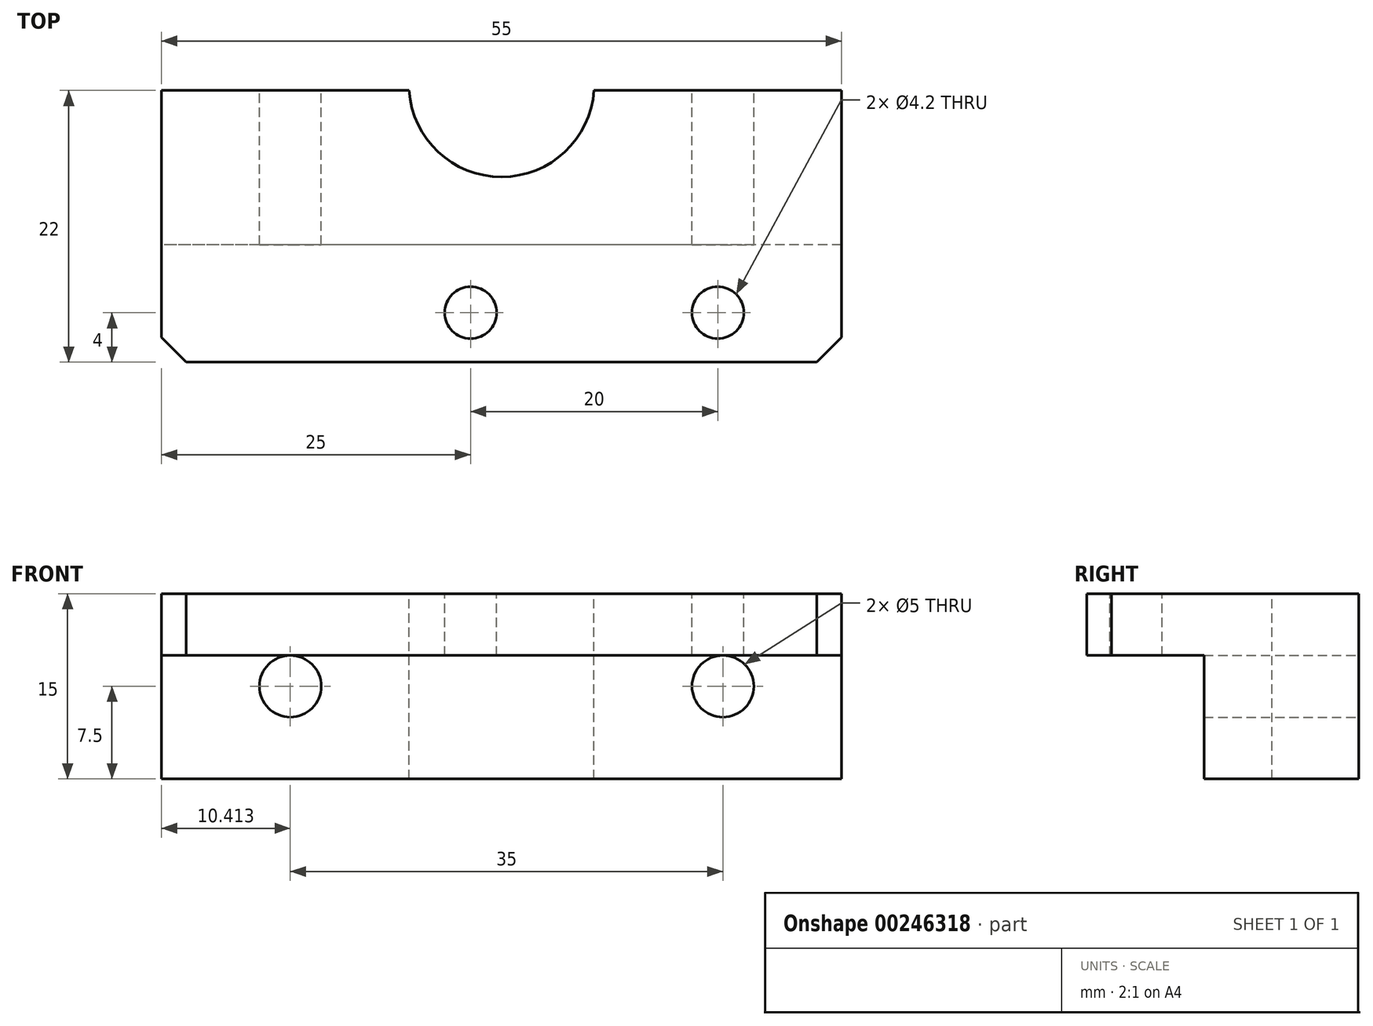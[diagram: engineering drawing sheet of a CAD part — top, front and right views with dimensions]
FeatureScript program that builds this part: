
annotation { "Feature Type Name" : "Feature", "Feature Type Description" : "" }
export const myFeature = defineFeature(function(context is Context, id is Id, definition is map)
    precondition{}
    {
        {
            var Q0;
            Q0=qCreatedBy(makeId("Right.planeOp"),FACE);
            var sketch = newSketch(context, id + "F0", { "sketchPlane" : qUnion([Q0])});
            skLineSegment(sketch, "E0", {"start": v(0, 0) * mm, "end": v(0, 15) * mm});
            skLineSegment(sketch, "E1", {"start": v(0, 15) * mm, "end": v(-22, 15) * mm});
            skLineSegment(sketch, "E2", {"start": v(-22, 15) * mm, "end": v(-22, 10) * mm});
            skLineSegment(sketch, "E3", {"start": v(-22, 10) * mm, "end": v(-12.5, 10) * mm});
            skLineSegment(sketch, "E4", {"start": v(-12.5, 10) * mm, "end": v(-12.5, 0) * mm});
            skLineSegment(sketch, "E5", {"start": v(-12.5, 0) * mm, "end": v(0, 0) * mm});
            skSolve(sketch);
        }
        {
            var Q0;
            Q0 = qSketchRegion(id + "F0", true);
            var Q1;
            Q1=makeQuery(id+"F0.imprint","IMPRINT",FACE,{"disambiguationData":[TD([[makeQuery(id+"F0.imprint","IMPRINT",EDGE,{"derivedFrom":sQuery(id+"F0.wireOp",EDGE,"E0")}),1.0]])]});
            extrude(context, id + "F1", {"entities" : qUnion([Q0, Q1]), "depth" : 55 * mm});
        }
        {
            var Q0;
            Q0=makeQuery(id+"F1.opExtrude","SWEPT_FACE",FACE,{"disambiguationData":[OSD([sQuery(id+"F0.wireOp",EDGE,"E1")])]});
            var sketch = newSketch(context, id + "F2", { "sketchPlane" : qUnion([Q0])});
            skCircle(sketch, "E6", {"center": v(27.5, 0.5) * mm, "radius": 7.5 * mm});
            skSolve(sketch);
        }
        {
            var Q0;
            {var subQ0=sQuery(id+"F2.wireOp",EDGE,"E6");var subQ1=makeQuery(id+"F1.opExtrude","SWEPT_EDGE",EDGE,{"disambiguationData":[OSD([sQuery(id+"F0.wireOp",EDGE,"E0"),sQuery(id+"F0.wireOp",EDGE,"E1")])]});var subQ2=makeQuery(id+"F2.imprint","INTERSECT",VERTEX,{"disambiguationData":[OD(0.0)],"derivedFrom":[subQ1,subQ0]});Q0=makeQuery(id+"F2.imprint","IMPRINT",FACE,{"disambiguationData":[TD([[makeQuery(id+"F2.imprint","IMPRINT",EDGE,{"disambiguationData":[TD([[subQ2,1.0]])],"derivedFrom":subQ0}),1.0]])]});}
            var Q1;
            {var subQ0=sQuery(id+"F2.wireOp",EDGE,"E6");var subQ1=makeQuery(id+"F1.opExtrude","SWEPT_EDGE",EDGE,{"disambiguationData":[OSD([sQuery(id+"F0.wireOp",EDGE,"E0"),sQuery(id+"F0.wireOp",EDGE,"E1")])]});var subQ2=makeQuery(id+"F2.imprint","INTERSECT",VERTEX,{"disambiguationData":[OD(0.0)],"derivedFrom":[subQ1,subQ0]});Q1=makeQuery(id+"F2.imprint","IMPRINT",FACE,{"disambiguationData":[TD([[makeQuery(id+"F2.imprint","IMPRINT",EDGE,{"disambiguationData":[TD([[subQ2,-1.0]])],"derivedFrom":subQ0}),1.0]])]});}
            extrude(context, id + "F3", {"entities" : qUnion([Q0, Q1]), "operationType" : NewBodyOperationType.REMOVE, "oppositeDirection" : true, "depth" : 60 * mm});
        }
        {
            var Q0;
            Q0=makeQuery(id+"F1.opExtrude","SWEPT_FACE",FACE,{"disambiguationData":[OSD([sQuery(id+"F0.wireOp",EDGE,"E1")])]});
            var sketch = newSketch(context, id + "F4", { "sketchPlane" : qUnion([Q0])});
            skPoint(sketch, "E7", {"position": v(45, -18) * mm});
            skPoint(sketch, "E8", {"position": v(25, -18) * mm});
            skSolve(sketch);
        }
        {
            var Q0;
            Q0=sQuery(id+"F4.wireOp",VERTEX,"E8");
            var Q1;
            Q1=sQuery(id+"F4.wireOp",VERTEX,"E7");
            var Q2;
            Q2=makeQuery(id+"F1.opExtrude","SWEPT_BODY",BODY,{"disambiguationData":[OSD([sQuery(id+"F0.wireOp",EDGE,"E0"),sQuery(id+"F0.wireOp",EDGE,"E1"),sQuery(id+"F0.wireOp",EDGE,"E2"),sQuery(id+"F0.wireOp",EDGE,"E3"),sQuery(id+"F0.wireOp",EDGE,"E4"),sQuery(id+"F0.wireOp",EDGE,"E5")])]});
            hole(context, id + "F5", {"style" : HoleStyle.SIMPLE, "endStyle" : HoleEndStyle.THROUGH, "standardTappedOrClearance" : lookupTablePath({ "standard" : "ISO", "engagement" : "75%", "pitch" : "0.8 mm", "size" : "M5", "type" : "Tapped" }), "standardBlindInLast" : lookupTablePath({ "standard" : "ISO", "engagement" : "75%", "pitch" : "0.8 mm", "size" : "M5", "type" : "Tapped" }), "holeDiameter" : 4.2 * mm, "showTappedDepth" : true, "tappedDepth" : 12 * mm, "tapClearance" : 3, "locations" : qUnion([Q0, Q1]), "scope" : qUnion([Q2]), "majorDiameter" : 5 * mm});
        }
        {
            var Q0;
            {var subQ0=sQuery(id+"F0.wireOp",EDGE,"E5");var subQ1=sQuery(id+"F0.wireOp",EDGE,"E1");var subQ2=sQuery(id+"F0.wireOp",EDGE,"E0");Q0=makeQuery(id+"F3.boolean.opBoolean","SPLIT",FACE,{"disambiguationData":[TD([makeQuery(id+"F1.opExtrude","CAP_FACE",FACE,{"disambiguationData":[OSD([subQ2,subQ1,sQuery(id+"F0.wireOp",EDGE,"E2"),sQuery(id+"F0.wireOp",EDGE,"E3"),sQuery(id+"F0.wireOp",EDGE,"E4"),subQ0])],"isStart":true})])],"derivedFrom":makeQuery(id+"F1.opExtrude","SWEPT_FACE",FACE,{"disambiguationData":[OSD([subQ2])]})});}
            var sketch = newSketch(context, id + "F6", { "sketchPlane" : qUnion([Q0])});
            skPoint(sketch, "E9", {"position": v(-10.41, 7.5) * mm});
            skPoint(sketch, "E9.positionSnap0", {"position": v(0, 7.5) * mm});
            skPoint(sketch, "E10", {"position": v(-45.41, 7.5) * mm});
            skPoint(sketch, "E10.positionSnap0", {"position": v(-20.02, 7.5) * mm});
            skSolve(sketch);
        }
        {
            var Q0;
            Q0=sQuery(id+"F6.wireOp",VERTEX,"E9");
            var Q1;
            Q1=sQuery(id+"F6.wireOp",VERTEX,"E10");
            var Q2;
            Q2=makeQuery(id+"F1.opExtrude","SWEPT_BODY",BODY,{"disambiguationData":[OSD([sQuery(id+"F0.wireOp",EDGE,"E0"),sQuery(id+"F0.wireOp",EDGE,"E1"),sQuery(id+"F0.wireOp",EDGE,"E2"),sQuery(id+"F0.wireOp",EDGE,"E3"),sQuery(id+"F0.wireOp",EDGE,"E4"),sQuery(id+"F0.wireOp",EDGE,"E5")])]});
            hole(context, id + "F7", {"style" : HoleStyle.SIMPLE, "endStyle" : HoleEndStyle.THROUGH, "standardTappedOrClearance" : lookupTablePath({ "standard" : "ISO", "engagement" : "75%", "pitch" : "1 mm", "size" : "M6", "type" : "Tapped" }), "standardBlindInLast" : lookupTablePath({ "standard" : "ISO", "engagement" : "75%", "pitch" : "1 mm", "size" : "M6", "type" : "Tapped" }), "holeDiameter" : 5 * mm, "showTappedDepth" : true, "tappedDepth" : 13 * mm, "tapClearance" : 3, "locations" : qUnion([Q0, Q1]), "scope" : qUnion([Q2]), "majorDiameter" : 6 * mm});
        }
        {
            var Q0;
            Q0=makeQuery(id+"F1.opExtrude","CAP_EDGE",EDGE,{"disambiguationData":[OSD([sQuery(id+"F0.wireOp",EDGE,"E2")])],"isStart":true});
            var Q1;
            Q1=makeQuery(id+"F1.opExtrude","CAP_EDGE",EDGE,{"disambiguationData":[OSD([sQuery(id+"F0.wireOp",EDGE,"E2")])],"isStart":false});
            chamfer(context, id + "F8", {"entities" : qUnion([Q0, Q1]), "chamferType" : ChamferType.OFFSET_ANGLE, "width" : 2 * mm, "oppositeDirection" : false, "angle" : 45 * degree, "tangentPropagation" : true});
        }
    });
